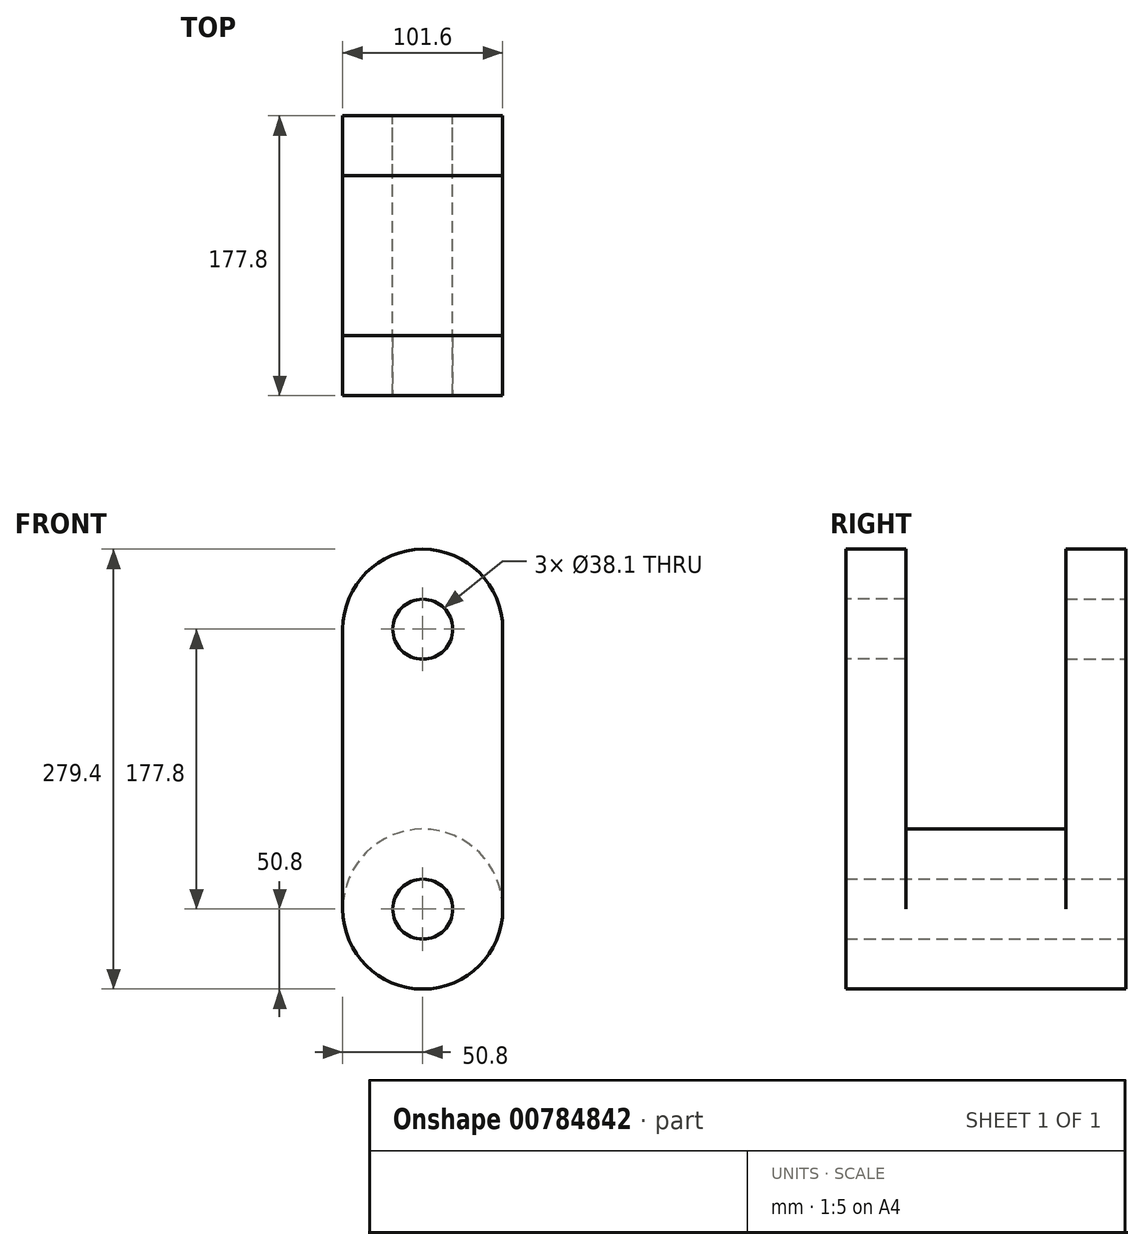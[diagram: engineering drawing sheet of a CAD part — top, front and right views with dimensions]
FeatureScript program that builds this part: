
annotation { "Feature Type Name" : "Feature", "Feature Type Description" : "" }
export const myFeature = defineFeature(function(context is Context, id is Id, definition is map)
    precondition{}
    {
        {
            var Q0;
            Q0=qCreatedBy(makeId("Front.planeOp"),FACE);
            var sketch = newSketch(context, id + "F0", { "sketchPlane" : qUnion([Q0])});
            skCircle(sketch, "E0", {"center": v(0, 0) * mm, "radius": 50.8 * mm});
            skCircle(sketch, "E1", {"center": v(0, 0) * mm, "radius": 19.05 * mm});
            skSolve(sketch);
        }
        {
            var Q0;
            Q0=makeQuery(id+"F0.imprint","IMPRINT",FACE,{"disambiguationData":[TD([[makeQuery(id+"F0.imprint","IMPRINT",EDGE,{"derivedFrom":sQuery(id+"F0.wireOp",EDGE,"E0")}),1.0]])]});
            extrude(context, id + "F1", {"entities" : qUnion([Q0]), "depth" : 177.8 * mm, "offsetDistance" : 25.4 * mm});
        }
        {
            var Q0;
            Q0=makeQuery(id+"F1.opExtrude","CAP_FACE",FACE,{"disambiguationData":[OSD([sQuery(id+"F0.wireOp",EDGE,"E0"),sQuery(id+"F0.wireOp",EDGE,"E1")])],"isStart":false});
            var sketch = newSketch(context, id + "F2", { "sketchPlane" : qUnion([Q0])});
            skArc(sketch, "E2", {"start": v(-50.8, 0) * mm, "mid": v(0, -50.8) * mm, "end": v(50.8, 0) * mm});
            skLineSegment(sketch, "E3", {"start": v(50.8, 0) * mm, "end": v(50.8, 177.8) * mm});
            skLineSegment(sketch, "E4", {"start": v(-50.8, 0) * mm, "end": v(-50.8, 177.8) * mm});
            skArc(sketch, "E5", {"start": v(50.8, 177.8) * mm, "mid": v(0, 228.6) * mm, "end": v(-50.8, 177.8) * mm});
            skSolve(sketch);
        }
        {
            var Q0;
            {var subQ0=sQuery(id+"F2.wireOp",EDGE,"E3");Q0=makeQuery(id+"F2.imprint","IMPRINT",FACE,{"disambiguationData":[TD([[makeQuery(id+"F2.imprint","IMPRINT",EDGE,{"derivedFrom":subQ0}),1.0]])]});}
            extrude(context, id + "F3", {"entities" : qUnion([Q0]), "operationType" : NewBodyOperationType.ADD, "oppositeDirection" : true, "depth" : 38.1 * mm, "offsetDistance" : 25.4 * mm});
        }
        {
            var Q0;
            Q0=makeQuery(id+"F1.opExtrude","CAP_FACE",FACE,{"disambiguationData":[OSD([sQuery(id+"F0.wireOp",EDGE,"E0"),sQuery(id+"F0.wireOp",EDGE,"E1")])],"isStart":true});
            var sketch = newSketch(context, id + "F4", { "sketchPlane" : qUnion([Q0])});
            skArc(sketch, "E6", {"start": v(-50.8, 0) * mm, "mid": v(0, -50.8) * mm, "end": v(50.8, 0) * mm});
            skLineSegment(sketch, "E7", {"start": v(50.8, 0) * mm, "end": v(50.8, 177.8) * mm});
            skLineSegment(sketch, "E8", {"start": v(-50.8, 0) * mm, "end": v(-50.8, 177.8) * mm});
            skArc(sketch, "E9", {"start": v(50.8, 177.8) * mm, "mid": v(0, 228.6) * mm, "end": v(-50.8, 177.8) * mm});
            skSolve(sketch);
        }
        {
            var Q0;
            {var subQ0=sQuery(id+"F4.wireOp",EDGE,"E7");Q0=makeQuery(id+"F4.imprint","IMPRINT",FACE,{"disambiguationData":[TD([[makeQuery(id+"F4.imprint","IMPRINT",EDGE,{"derivedFrom":subQ0}),1.0]])]});}
            extrude(context, id + "F5", {"entities" : qUnion([Q0]), "operationType" : NewBodyOperationType.ADD, "oppositeDirection" : true, "depth" : 38.1 * mm, "offsetDistance" : 25.4 * mm});
        }
        {
            var Q0;
            {var subQ0=sQuery(id+"F0.wireOp",EDGE,"E0");Q0=makeQuery(id+"F5.boolean.opBoolean","MERGE",FACE,{"derivedFrom":[makeQuery(id+"F1.opExtrude","CAP_FACE",FACE,{"disambiguationData":[OSD([subQ0,sQuery(id+"F0.wireOp",EDGE,"E1")])],"isStart":true}),makeQuery(id+"F5.opExtrude","CAP_FACE",FACE,{"disambiguationData":[OSD([subQ0,sQuery(id+"F4.wireOp",EDGE,"E7"),sQuery(id+"F4.wireOp",EDGE,"E8"),sQuery(id+"F4.wireOp",EDGE,"E9")])],"isStart":true})]});}
            var sketch = newSketch(context, id + "F6", { "sketchPlane" : qUnion([Q0])});
            skCircle(sketch, "E10", {"center": v(0, 177.8) * mm, "radius": 19.05 * mm});
            skSolve(sketch);
        }
        {
            var Q0;
            Q0=makeQuery(id+"F6.imprint","IMPRINT",FACE,{"disambiguationData":[TD([[makeQuery(id+"F6.imprint","IMPRINT",EDGE,{"derivedFrom":sQuery(id+"F6.wireOp",EDGE,"E10")}),1.0]])]});
            extrude(context, id + "F7", {"entities" : qUnion([Q0]), "operationType" : NewBodyOperationType.REMOVE, "oppositeDirection" : true, "depth" : 66.8 * mm, "offsetDistance" : 25.4 * mm});
        }
        {
            var Q0;
            {var subQ0=sQuery(id+"F0.wireOp",EDGE,"E0");Q0=makeQuery(id+"F3.boolean.opBoolean","MERGE",FACE,{"derivedFrom":[makeQuery(id+"F1.opExtrude","CAP_FACE",FACE,{"disambiguationData":[OSD([subQ0,sQuery(id+"F0.wireOp",EDGE,"E1")])],"isStart":false}),makeQuery(id+"F3.opExtrude","CAP_FACE",FACE,{"disambiguationData":[OSD([subQ0,sQuery(id+"F2.wireOp",EDGE,"E3"),sQuery(id+"F2.wireOp",EDGE,"E4"),sQuery(id+"F2.wireOp",EDGE,"E5")])],"isStart":true})]});}
            var sketch = newSketch(context, id + "F8", { "sketchPlane" : qUnion([Q0])});
            skCircle(sketch, "E11", {"center": v(0, 177.8) * mm, "radius": 19.05 * mm});
            skSolve(sketch);
        }
        {
            var Q0;
            Q0=makeQuery(id+"F8.imprint","IMPRINT",FACE,{"disambiguationData":[TD([[makeQuery(id+"F8.imprint","IMPRINT",EDGE,{"derivedFrom":sQuery(id+"F8.wireOp",EDGE,"E11")}),1.0]])]});
            extrude(context, id + "F9", {"entities" : qUnion([Q0]), "operationType" : NewBodyOperationType.REMOVE, "oppositeDirection" : true, "depth" : 106.68 * mm, "offsetDistance" : 25.4 * mm});
        }
    });
